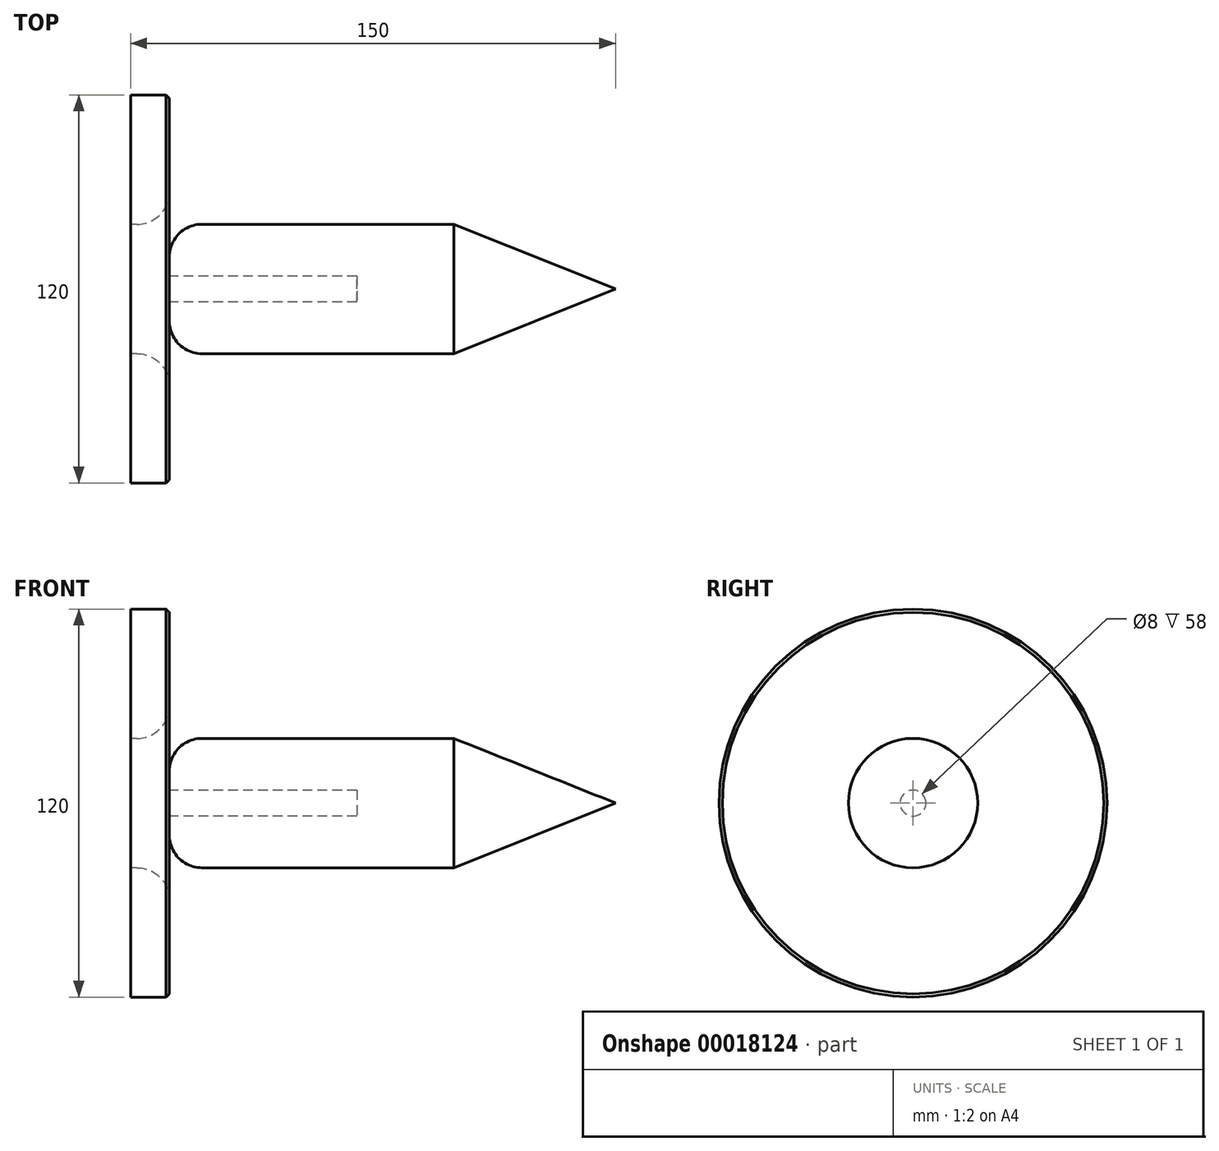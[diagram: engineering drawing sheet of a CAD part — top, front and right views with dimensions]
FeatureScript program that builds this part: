
annotation { "Feature Type Name" : "Feature", "Feature Type Description" : "" }
export const myFeature = defineFeature(function(context is Context, id is Id, definition is map)
    precondition{}
    {
        {
            var Q0;
            Q0=qCreatedBy(makeId("Front.planeOp"),FACE);
            var sketch = newSketch(context, id + "F0", { "sketchPlane" : qUnion([Q0])});
            skLineSegment(sketch, "E0", {"start": v(0, 0) * mm, "end": v(178.2, 0) * mm, "construction": true});
            skLineSegment(sketch, "E1.bottom", {"start": v(0, 0) * mm, "end": v(12, 0) * mm});
            skLineSegment(sketch, "E1.top", {"start": v(0, 60) * mm, "end": v(12, 60) * mm});
            skLineSegment(sketch, "E1.left", {"start": v(0, 0) * mm, "end": v(0, 60) * mm});
            skLineSegment(sketch, "E1.right", {"start": v(12, 0) * mm, "end": v(12, 60) * mm});
            skLineSegment(sketch, "E2.bottom", {"start": v(0, 20) * mm, "end": v(100, 20) * mm});
            skLineSegment(sketch, "E2.top", {"start": v(0, 0) * mm, "end": v(100, 0) * mm});
            skLineSegment(sketch, "E2.left", {"start": v(0, 20) * mm, "end": v(0, 0) * mm});
            skLineSegment(sketch, "E2.right", {"start": v(100, 20) * mm, "end": v(100, 0) * mm});
            skLineSegment(sketch, "E3", {"start": v(100, 20) * mm, "end": v(150, 0) * mm});
            skLineSegment(sketch, "E4", {"start": v(150, 0) * mm, "end": v(100, 0) * mm});
            skSolve(sketch);
        }
        {
            var Q0;
            {var subQ4=sQuery(id+"F0.wireOp",EDGE,"E1.top");Q0=makeQuery(id+"F0.imprint","IMPRINT",FACE,{"disambiguationData":[TD([[makeQuery(id+"F0.imprint","IMPRINT",EDGE,{"derivedFrom":subQ4}),-1.0]])]});}
            var Q1;
            {var subQ0=sQuery(id+"F0.wireOp",EDGE,"E2.left");Q1=makeQuery(id+"F0.imprint","IMPRINT",FACE,{"disambiguationData":[TD([[makeQuery(id+"F0.imprint","IMPRINT",EDGE,{"derivedFrom":subQ0}),1.0]])]});}
            var Q2;
            {var subQ0=sQuery(id+"F0.wireOp",EDGE,"E2.right");Q2=makeQuery(id+"F0.imprint","IMPRINT",FACE,{"disambiguationData":[TD([[makeQuery(id+"F0.imprint","IMPRINT",EDGE,{"derivedFrom":subQ0}),-1.0]])]});}
            var Q3;
            Q3=makeQuery(id+"F0.imprint","IMPRINT",FACE,{"disambiguationData":[TD([[makeQuery(id+"F0.imprint","IMPRINT",EDGE,{"derivedFrom":sQuery(id+"F0.wireOp",EDGE,"E2.right")}),1.0]])]});
            var Q4;
            Q4=sQuery(id+"F0.wireOp",EDGE,"E0");
            revolve(context, id + "F1", {"entities" : qUnion([Q0, Q1, Q2, Q3]), "axis" : qUnion([Q4]), "revolveType" : RevolveType.FULL});
        }
        {
            var Q0;
            Q0=makeQuery(id+"F1.opRevolve","SWEPT_EDGE",EDGE,{"disambiguationData":[OSD([sQuery(id+"F0.wireOp",EDGE,"E1.right"),sQuery(id+"F0.wireOp",EDGE,"E2.bottom")])]});
            fillet(context, id + "F2", {"entities" : qUnion([Q0]), "radius" : 10 * mm, "tangentPropagation" : true, "allowEdgeOverflow" : false});
        }
        {
            var Q0;
            Q0=makeQuery(id+"F1.opRevolve","SWEPT_EDGE",EDGE,{"disambiguationData":[OSD([sQuery(id+"F0.wireOp",EDGE,"E1.top"),sQuery(id+"F0.wireOp",EDGE,"E1.right")])]});
            chamfer(context, id + "F3", {"entities" : qUnion([Q0]), "width" : 1 * mm, "tangentPropagation" : true});
        }
        {
            var Q0;
            Q0=makeQuery(id+"F1.opRevolve","SWEPT_FACE",FACE,{"disambiguationData":[OSD([sQuery(id+"F0.wireOp",EDGE,"E1.left"),sQuery(id+"F0.wireOp",EDGE,"E2.left")])]});
            var sketch = newSketch(context, id + "F4", { "sketchPlane" : qUnion([Q0])});
            skCircle(sketch, "E5", {"center": v(0, 0) * mm, "radius": 4 * mm});
            skSolve(sketch);
        }
        {
            var Q0;
            Q0=makeQuery(id+"F4.imprint","IMPRINT",FACE,{"disambiguationData":[TD([[makeQuery(id+"F4.imprint","IMPRINT",EDGE,{"derivedFrom":sQuery(id+"F4.wireOp",EDGE,"E5")}),1.0]])]});
            extrude(context, id + "F5", {"entities" : qUnion([Q0]), "operationType" : NewBodyOperationType.REMOVE, "oppositeDirection" : true, "depth" : 70 * mm});
        }
    });
